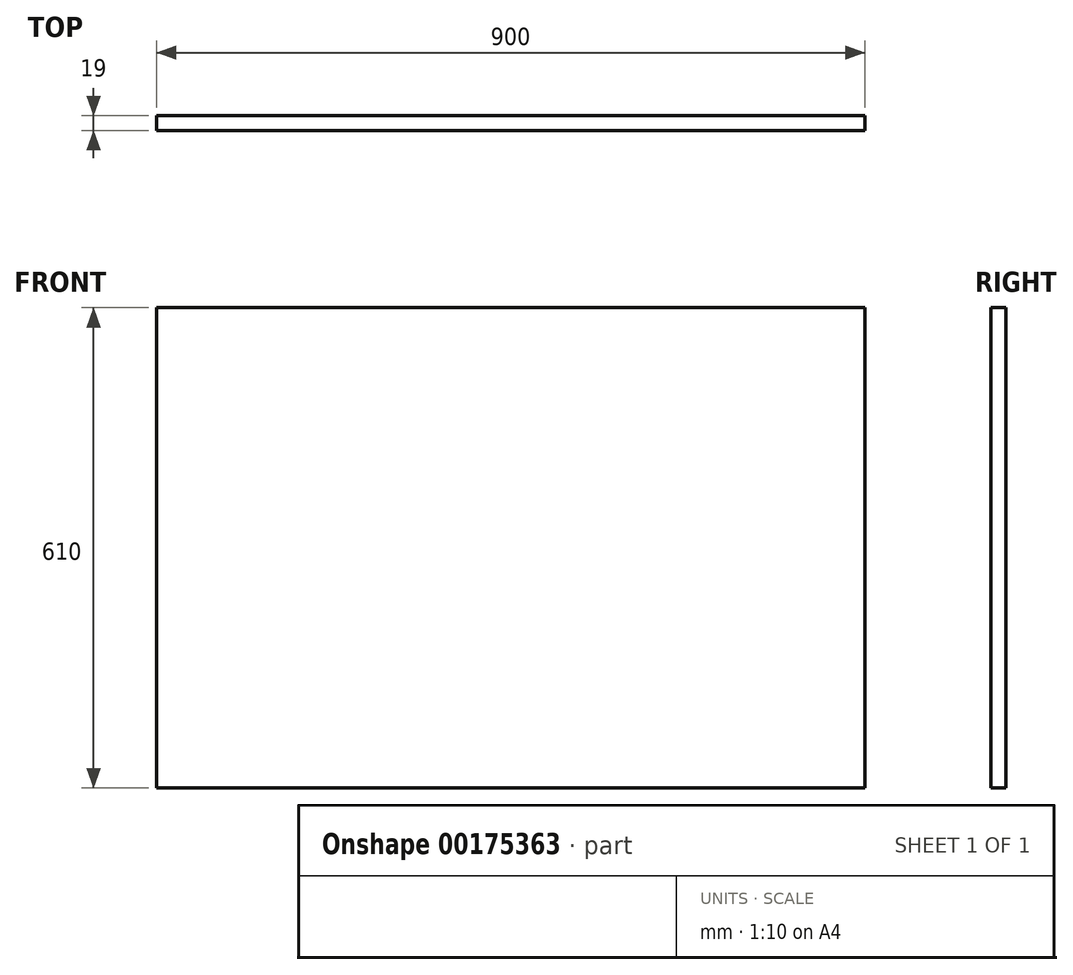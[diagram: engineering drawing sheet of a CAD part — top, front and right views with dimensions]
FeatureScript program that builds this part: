
annotation { "Feature Type Name" : "Feature", "Feature Type Description" : "" }
export const myFeature = defineFeature(function(context is Context, id is Id, definition is map)
    precondition{}
    {
        {
            var Q0;
            Q0=qCreatedBy(makeId("Front.planeOp"),FACE);
            var sketch = newSketch(context, id + "F0", { "sketchPlane" : qUnion([Q0])});
            skLineSegment(sketch, "E0.bottom", {"start": v(-11432.74, -6001.33) * mm, "end": v(-10532.74, -6001.33) * mm});
            skLineSegment(sketch, "E0.top", {"start": v(-11432.74, -6611.33) * mm, "end": v(-10532.74, -6611.33) * mm});
            skLineSegment(sketch, "E0.left", {"start": v(-11432.74, -6001.33) * mm, "end": v(-11432.74, -6611.33) * mm});
            skLineSegment(sketch, "E0.right", {"start": v(-10532.74, -6001.33) * mm, "end": v(-10532.74, -6611.33) * mm});
            skSolve(sketch);
        }
        {
            var Q0;
            Q0=makeQuery(id+"F0.imprint","IMPRINT",FACE,{"disambiguationData":[TD([[makeQuery(id+"F0.imprint","IMPRINT",EDGE,{"derivedFrom":sQuery(id+"F0.wireOp",EDGE,"E0.bottom")}),-1.0]])]});
            extrude(context, id + "F1", {"entities" : qUnion([Q0]), "depth" : 19 * mm});
        }
    });
